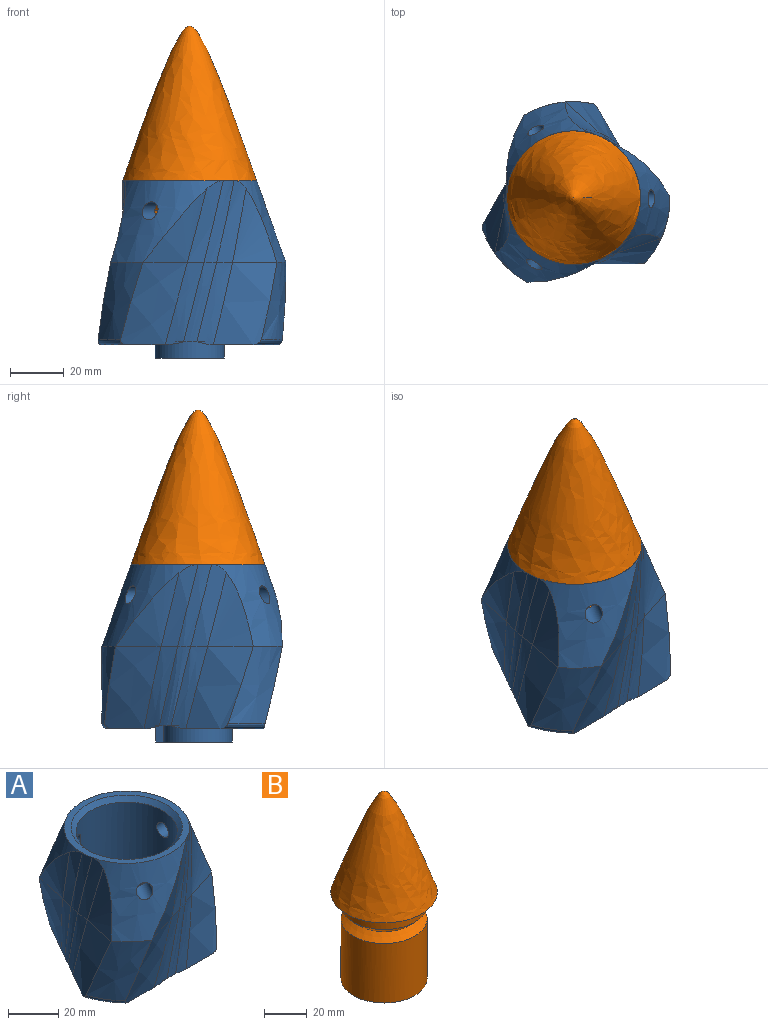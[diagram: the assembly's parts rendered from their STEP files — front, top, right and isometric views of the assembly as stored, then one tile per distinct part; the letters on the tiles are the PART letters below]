
ASSEMBLY  parts=2 mates=1
PART A: 59 faces, bbox 76.5x72.6x102.4 mm
  f0: cylinder r=20.2mm len=48mm, axis (0,0,1), area 5988.6mm2, adj f51,f54,f55,f56,f57
  f1: cone r=5.67mm half-angle=19.8deg, axis (0,0,-1), area 869.8mm2, adj f14,f32,f33,f34,f35,f47,f56
  f2: cone r=5.67mm half-angle=19.8deg, axis (0,0,-1), area 869.8mm2, adj f17,f37,f38,f39,f40,f47,f55
  f3: cone r=5.67mm half-angle=19.8deg, axis (0,0,-1), area 874.8mm2, adj f11,f27,f28,f29,f30,f47,f54
  f4: plane 50.05x50mm, normal (0,0,-1), area 1420.5mm2, adj f7,f8,f19,f44,f45,f46,f48,f49
  f5: plane 33.99x14.32mm, normal (0,0,-1), area 213.8mm2, adj f16,f18,f20,f21,f41,f46
  f6: plane 29.44x24.55mm, normal (0,0,-1), area 213.8mm2, adj f10,f12,f24,f25,f43,f45
  f7: bspline ~43.86x19.6mm, area 148.3mm2, adj f4,f23,f24,f31
  f8: bspline ~43.86x14.74mm, area 148.3mm2, adj f4,f21,f22,f36
  f9: plane 29.44x24.5mm, normal (0,0,-1), area 213.8mm2, adj f13,f15,f22,f23,f42,f44
  f10: bspline ~43.86x32.62mm, area 541.6mm2, adj f6,f11,f25,f28,f43
  f11: bspline ~43.86x23.02mm, area 468.9mm2, adj f3,f10,f12,f43
  f12: bspline ~43.86x32.74mm, area 538.4mm2, adj f6,f11,f24,f29,f43
  f13: bspline ~43.86x29.67mm, area 541.6mm2, adj f9,f14,f23,f33,f42
  f14: bspline ~43.86x30.01mm, area 468.9mm2, adj f1,f13,f15,f42
  f15: bspline ~43.86x28.16mm, area 538.4mm2, adj f9,f14,f22,f34,f42
  f16: bspline ~30.7x19.96mm, area 541.6mm2, adj f5,f17,f21,f38,f41
  f17: bspline ~43.86x30.62mm, area 468.9mm2, adj f2,f16,f18,f41
  f18: bspline ~43.86x28.55mm, area 538.4mm2, adj f5,f17,f20,f39,f41
  f19: bspline ~43.86x19.21mm, area 148.3mm2, adj f4,f20,f25,f26
  f20: bspline ~42.73x13.58mm, area 194.6mm2, adj f5,f18,f19,f40,f46
  f21: bspline ~40.16x11mm, area 194.3mm2, adj f5,f8,f16,f37,f46
  f22: bspline ~42.73x13.22mm, area 194.6mm2, adj f8,f9,f15,f35,f44
  f23: bspline ~40.16x13.92mm, area 194.3mm2, adj f7,f9,f13,f32,f44
  f24: bspline ~42.73x15.47mm, area 194.6mm2, adj f6,f7,f12,f30,f45
  f25: bspline ~40.16x14.39mm, area 194.3mm2, adj f6,f10,f19,f27,f45
  f26: bspline ~43.86x15.95mm, area 153.2mm2, adj f19,f27,f40,f47
  f27: bspline ~66.67x22.13mm, area 189.1mm2, adj f3,f25,f26,f28,f47
  f28: bspline ~27.47x24.44mm, area 242.5mm2, adj f3,f10,f27
  f29: bspline ~43.86x28mm, area 242.6mm2, adj f3,f12,f30
  f30: bspline ~30.56x13.43mm, area 189.2mm2, adj f3,f24,f29,f31,f47
  f31: bspline ~43.86x13.69mm, area 153.1mm2, adj f7,f30,f32,f47
  f32: bspline ~30.56x11.53mm, area 189.1mm2, adj f1,f23,f31,f33,f47
  f33: bspline ~27.47x19.53mm, area 242.5mm2, adj f1,f13,f32
  f34: bspline ~43.86x20.58mm, area 242.6mm2, adj f1,f15,f35
  f35: bspline ~30.56x10.61mm, area 189.2mm2, adj f1,f22,f34,f36,f47
  f36: bspline ~30.56x10.64mm, area 153.2mm2, adj f8,f35,f37,f47
  f37: bspline ~66.67x22.54mm, area 189.1mm2, adj f2,f21,f36,f38,f47
  f38: bspline ~27.47x22.79mm, area 242.5mm2, adj f2,f16,f37
  f39: bspline ~43.86x28.04mm, area 242.6mm2, adj f2,f18,f40
  f40: bspline ~66.67x23.05mm, area 189.2mm2, adj f2,f20,f26,f39,f47
  f41: bspline ~31.33x5.49mm, area 56.1mm2, adj f5,f16,f17,f18
  f42: bspline ~28.87x15.09mm, area 56.1mm2, adj f9,f13,f14,f15
  f43: bspline ~28.74x15.4mm, area 56.1mm2, adj f6,f10,f11,f12
  f44: torus R=26mm, axis (0,0,1), area 66.1mm2, adj f4,f9,f22,f23
  f45: torus R=26mm, axis (0,0,1), area 66.1mm2, adj f4,f6,f24,f25
  f46: torus R=26mm, axis (0,0,1), area 66.1mm2, adj f4,f5,f20,f21
  f47: plane 50.01x50.01mm, normal (0,0,1), area 415.3mm2, adj f1,f2,f3,f26,f27,f30,f31,f32
  f48: plane 6x2.86mm, normal (0.95,-0.3,0), area 18mm2, adj f4,f49,f53,f58
  f49: plane 7.44x6mm, normal (0.3,0.95,0), area 46.8mm2, adj f4,f48,f50,f58
  f50: plane 6x2.86mm, normal (-0.95,0.3,0), area 18mm2, adj f4,f49,f53,f58
  f51: plane 40.4x40.4mm, normal (0,0,1), area 961.4mm2, adj f0,f52
  f52: cylinder r=10.1mm len=20.2mm, axis (0,0,-1), area 1031.9mm2, adj f51,f58
  f53: cylinder r=12.9mm len=25.8mm, axis (0,0,-1), area 438.8mm2, adj f4,f48,f50,f58
  f54: cylinder r=3.32mm len=12.22mm, axis (0.51,0.86,0), area 200.6mm2, adj f0,f3
  f55: cylinder r=3.32mm len=11.12mm, axis (0.49,-0.87,0), area 187.6mm2, adj f0,f2
  f56: cylinder r=3.32mm len=9.62mm, axis (-1,0.01,0), area 196.3mm2, adj f0,f1
  f57: cone r=20.2mm half-angle=45deg, axis (0,0,1), area 376.8mm2, adj f0,f47
  f58: plane 28.66x25.8mm, normal (0,0,-1), area 222.6mm2, adj f48,f49,f50,f52,f53
PART B: 15 faces, bbox 150x150x149.4 mm
  f0: cylinder r=20.2mm len=40.4mm, axis (0,0,1), area 4332.7mm2, adj f1,f10
  f1: plane 40.4x40.4mm, normal (0,0,-1), area 492mm2, adj f0,f2,f3,f4,f5,f6,f7
  f2: plane 29.4x15.1mm, normal (-0.87,0.5,0), area 512.6mm2, adj f1,f3,f6,f8
  f3: plane 29.4x15.1mm, normal (-0.87,-0.5,0), area 512.6mm2, adj f1,f2,f4,f8
  f4: plane 29.4x17.44mm, normal (0,-1,0), area 512.6mm2, adj f1,f3,f5,f8
  f5: plane 29.4x15.1mm, normal (0.87,-0.5,0), area 512.6mm2, adj f1,f4,f7,f8
  f6: plane 29.4x17.44mm, normal (0,1,0), area 512.6mm2, adj f1,f2,f7,f8
  f7: plane 29.4x15.1mm, normal (0.87,0.5,0), area 512.6mm2, adj f1,f5,f6,f8
  f8: plane 34.87x30.2mm, normal (0,0,-1), area 789.8mm2, adj f2,f3,f4,f5,f6,f7
  f9: cone r=16.2mm half-angle=45deg, axis (0,0,1), area 646.9mm2, adj f10,f13
  f10: cone r=20.2mm half-angle=45deg, axis (0,0,-1), area 646.9mm2, adj f0,f9
  f11: revolved ~50x25mm, area 0mm2, adj f12
  f12: plane 150x150mm, normal (0,0,-1), area 415.2mm2, adj f11,f14
  f13: cylinder r=20.2mm len=40.4mm, axis (0,0,1), area 667.9mm2, adj f9,f14
  f14: cone r=22.2mm half-angle=45deg, axis (0,0,1), area 376.8mm2, adj f12,f13
PLACE A at identity fixed
PLACE B t=(0,0,61.26)mm
MATE slider B.f0 <-> A.f0  axis (0,0,1) through (0,0,59.26)mm
